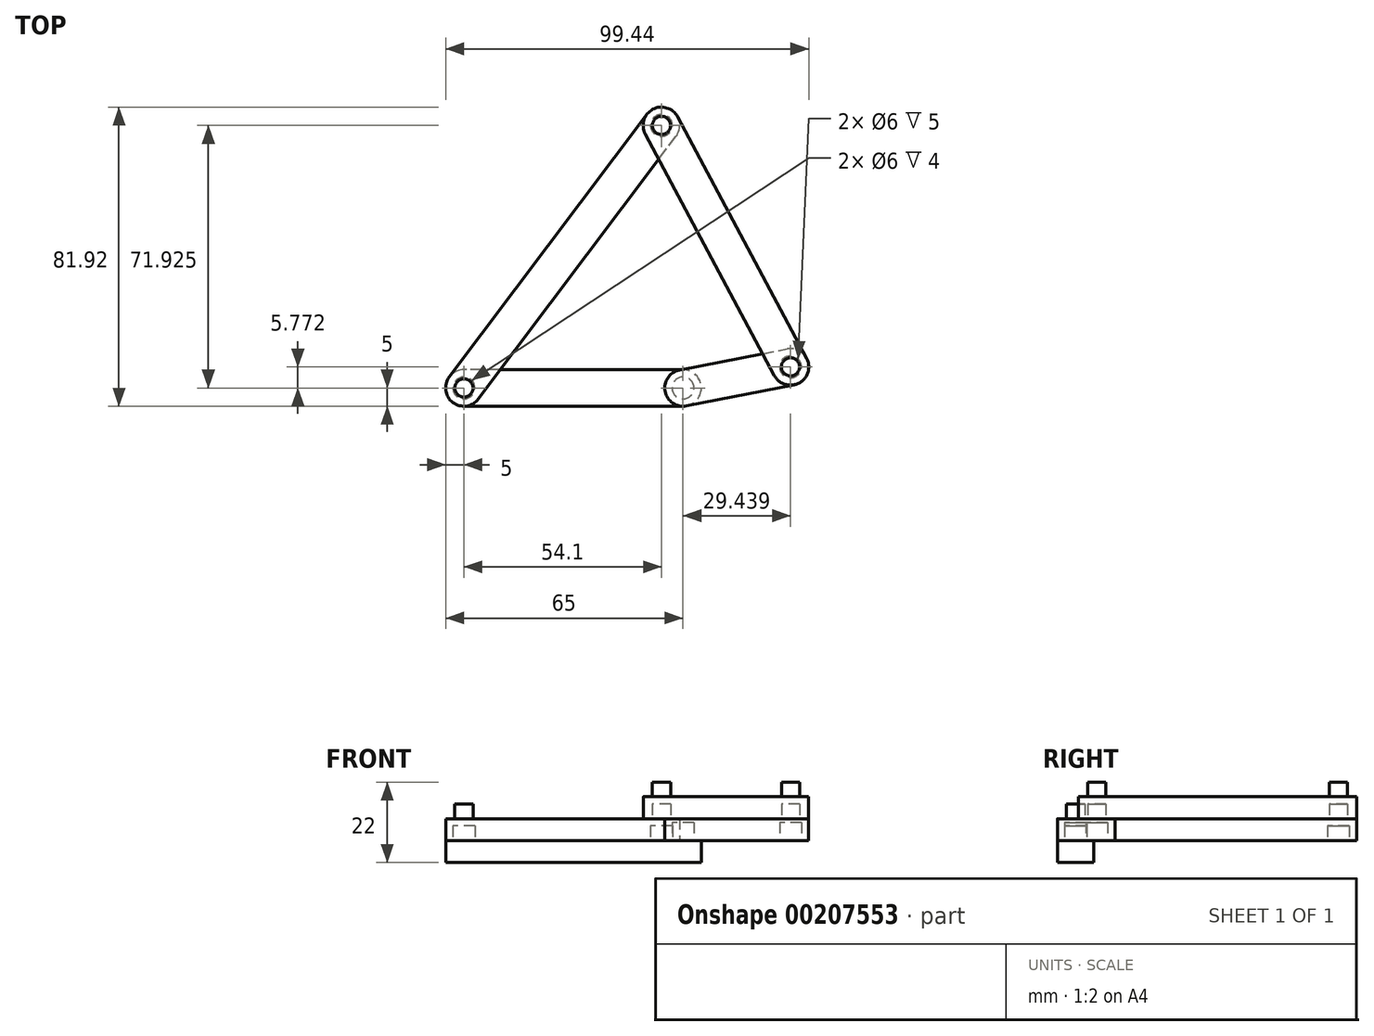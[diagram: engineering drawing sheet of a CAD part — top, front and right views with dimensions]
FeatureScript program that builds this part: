
annotation { "Feature Type Name" : "Feature", "Feature Type Description" : "" }
export const myFeature = defineFeature(function(context is Context, id is Id, definition is map)
    precondition{}
    {
        {
            var Q0;
            Q0=qCreatedBy(makeId("Top.planeOp"),FACE);
            var sketch = newSketch(context, id + "F0", { "sketchPlane" : qUnion([Q0])});
            skLineSegment(sketch, "E0", {"start": v(0, 0) * mm, "end": v(29.44, 5.77) * mm, "construction": true});
            skLineSegment(sketch, "E1", {"start": v(0, 0) * mm, "end": v(-60, 0) * mm, "construction": true});
            skLineSegment(sketch, "E2", {"start": v(-60, 0) * mm, "end": v(-5.9, 71.92) * mm, "construction": true});
            skLineSegment(sketch, "E3", {"start": v(-5.9, 71.92) * mm, "end": v(29.44, 5.77) * mm, "construction": true});
            skSolve(sketch);
        }
        {
            assignVariable(context, id + "F1", {"name" : "HEIGHT", "anyValue" : 6});
        }
        {
            var Q0;
            Q0=qCreatedBy(makeId("Top.planeOp"),FACE);
            cPlane(context, id + "F2", {"entities" : qUnion([Q0]), "cplaneType" : CPlaneType.OFFSET, "offset" : (getVariable(context, 'HEIGHT')) * mm, "width" : 150 * mm, "height" : 150 * mm});
        }
        {
            var Q0;
            Q0=qCreatedBy(id+"F2.planeOp",FACE);
            cPlane(context, id + "F3", {"entities" : qUnion([Q0]), "cplaneType" : CPlaneType.OFFSET, "offset" : (getVariable(context, 'HEIGHT')) * mm, "width" : 150 * mm, "height" : 150 * mm});
        }
        {
            var Q0;
            Q0=qCreatedBy(id+"F3.planeOp",FACE);
            cPlane(context, id + "F4", {"entities" : qUnion([Q0]), "cplaneType" : CPlaneType.OFFSET, "offset" : (getVariable(context, 'HEIGHT')) * mm, "width" : 150 * mm, "height" : 150 * mm});
        }
        {
            var Q0;
            Q0=qCreatedBy(makeId("Top.planeOp"),FACE);
            var sketch = newSketch(context, id + "F5", { "sketchPlane" : qUnion([Q0])});
            skLineSegment(sketch, "E4.JFF.JFF", {"start": v(0, 0) * mm, "end": v(-60, 0) * mm, "construction": true});
            skArc(sketch, "E4.0.startCap", {"start": v(0, 5) * mm, "mid": v(5, 0) * mm, "end": v(0, -5) * mm});
            skArc(sketch, "E4.0.endCap", {"start": v(-60, -5) * mm, "mid": v(-65, 0) * mm, "end": v(-60, 5) * mm});
            skLineSegment(sketch, "E4.0.left", {"start": v(0, -5) * mm, "end": v(-60, -5) * mm});
            skLineSegment(sketch, "E4.0.right", {"start": v(0, 5) * mm, "end": v(-60, 5) * mm});
            skSolve(sketch);
        }
        {
            var Q0;
            Q0=qSketchRegion(id+"F5",true);
            extrude(context, id + "F6", {"entities" : qUnion([Q0]), "depth" : (getVariable(context, 'HEIGHT')) * mm});
        }
        {
            var Q0;
            Q0=qCreatedBy(makeId("Top.planeOp"),FACE);
            var sketch = newSketch(context, id + "F7", { "sketchPlane" : qUnion([Q0])});
            skCircle(sketch, "E5", {"center": v(-60, 0) * mm, "radius": 2.5 * mm});
            skCircle(sketch, "E6", {"center": v(0, 0) * mm, "radius": 2.5 * mm});
            skSolve(sketch);
        }
        {
            var Q0;
            Q0=qSketchRegion(id+"F7",true);
            extrude(context, id + "F8", {"entities" : qUnion([Q0]), "operationType" : NewBodyOperationType.ADD, "depth" : (getVariable(context, 'HEIGHT') * 2 - 2) * mm});
        }
        {
            var Q0;
            Q0=qCreatedBy(makeId("Top.planeOp"),FACE);
            var sketch = newSketch(context, id + "F9", { "sketchPlane" : qUnion([Q0])});
            skCircle(sketch, "E7", {"center": v(-60, 0) * mm, "radius": 3 * mm});
            skCircle(sketch, "E8", {"center": v(0, 0) * mm, "radius": 3 * mm});
            skSolve(sketch);
        }
        {
            var Q0;
            Q0 = qSketchRegion(id + "F9", true);
            extrude(context, id + "F10", {"entities" : qUnion([Q0]), "operationType" : NewBodyOperationType.ADD, "depth" : (getVariable(context, 'HEIGHT') - 1) * mm});
        }
        {
            var Q0;
            Q0=qCreatedBy(id+"F2.planeOp",FACE);
            var sketch = newSketch(context, id + "F11", { "sketchPlane" : qUnion([Q0])});
            skLineSegment(sketch, "E9.JFB.JFB", {"start": v(0, 0) * mm, "end": v(29.44, 5.77) * mm, "construction": true});
            skArc(sketch, "E9.0.startCap", {"start": v(0.96, -4.9) * mm, "mid": v(-4.9, -0.96) * mm, "end": v(-0.96, 4.9) * mm});
            skArc(sketch, "E9.0.endCap", {"start": v(28.48, 10.68) * mm, "mid": v(34.35, 6.73) * mm, "end": v(30.4, 0.87) * mm});
            skLineSegment(sketch, "E9.0.left", {"start": v(-0.96, 4.9) * mm, "end": v(28.48, 10.68) * mm});
            skLineSegment(sketch, "E9.0.right", {"start": v(0.96, -4.9) * mm, "end": v(30.4, 0.87) * mm});
            skSolve(sketch);
        }
        {
            var Q0;
            Q0=qSketchRegion(id+"F11",true);
            extrude(context, id + "F12", {"entities" : qUnion([Q0]), "depth" : (getVariable(context, 'HEIGHT')) * mm});
        }
        {
            var Q0;
            Q0=qCreatedBy(id+"F3.planeOp",FACE);
            var sketch = newSketch(context, id + "F13", { "sketchPlane" : qUnion([Q0])});
            skCircle(sketch, "E10", {"center": v(29.44, 5.77) * mm, "radius": 2.5 * mm});
            skSolve(sketch);
        }
        {
            var Q0;
            Q0 = qSketchRegion(id + "F13", true);
            extrude(context, id + "F14", {"entities" : qUnion([Q0]), "operationType" : NewBodyOperationType.ADD, "depth" : (getVariable(context, 'HEIGHT') - 2) * mm});
        }
        {
            var Q0;
            Q0=qCreatedBy(id+"F2.planeOp",FACE);
            var sketch = newSketch(context, id + "F15", { "sketchPlane" : qUnion([Q0])});
            skCircle(sketch, "E11", {"center": v(0, 0) * mm, "radius": 3 * mm});
            skCircle(sketch, "E12", {"center": v(29.44, 5.77) * mm, "radius": 3 * mm});
            skSolve(sketch);
        }
        {
            var Q0;
            Q0 = qSketchRegion(id + "F15", true);
            extrude(context, id + "F16", {"entities" : qUnion([Q0]), "operationType" : NewBodyOperationType.REMOVE, "depth" : (getVariable(context, 'HEIGHT') - 1) * mm});
        }
        {
            var Q0;
            Q0=qCreatedBy(id+"F2.planeOp",FACE);
            var sketch = newSketch(context, id + "F17", { "sketchPlane" : qUnion([Q0])});
            skLineSegment(sketch, "E13.JFJ.JFJ", {"start": v(-60, 0) * mm, "end": v(-5.9, 71.92) * mm, "construction": true});
            skArc(sketch, "E13.0.startCap", {"start": v(-56, -3) * mm, "mid": v(-63, -4) * mm, "end": v(-64, 3) * mm});
            skArc(sketch, "E13.0.endCap", {"start": v(-9.9, 74.93) * mm, "mid": v(-2.9, 75.92) * mm, "end": v(-1.9, 68.92) * mm});
            skLineSegment(sketch, "E13.0.left", {"start": v(-64, 3) * mm, "end": v(-9.9, 74.93) * mm});
            skLineSegment(sketch, "E13.0.right", {"start": v(-56, -3) * mm, "end": v(-1.9, 68.92) * mm});
            skSolve(sketch);
        }
        {
            var Q0;
            Q0=qSketchRegion(id+"F17",true);
            extrude(context, id + "F18", {"entities" : qUnion([Q0]), "depth" : (getVariable(context, 'HEIGHT')) * mm});
        }
        {
            var Q0;
            Q0=qCreatedBy(id+"F3.planeOp",FACE);
            var sketch = newSketch(context, id + "F19", { "sketchPlane" : qUnion([Q0])});
            skCircle(sketch, "E14", {"center": v(-5.9, 71.92) * mm, "radius": 2.5 * mm});
            skCircle(sketch, "E15", {"center": v(-60, 0) * mm, "radius": 2.5 * mm});
            skSolve(sketch);
        }
        {
            var Q0;
            Q0 = qSketchRegion(id + "F19", true);
            extrude(context, id + "F20", {"entities" : qUnion([Q0]), "operationType" : NewBodyOperationType.ADD, "depth" : (getVariable(context, 'HEIGHT') - 2) * mm});
        }
        {
            var Q0;
            Q0=qCreatedBy(id+"F2.planeOp",FACE);
            var sketch = newSketch(context, id + "F21", { "sketchPlane" : qUnion([Q0])});
            skCircle(sketch, "E16", {"center": v(-60, 0) * mm, "radius": 3 * mm});
            skCircle(sketch, "E17", {"center": v(-5.9, 71.92) * mm, "radius": 3 * mm});
            skSolve(sketch);
        }
        {
            var Q0;
            Q0 = qSketchRegion(id + "F21", true);
            extrude(context, id + "F22", {"entities" : qUnion([Q0]), "operationType" : NewBodyOperationType.REMOVE, "depth" : (getVariable(context, 'HEIGHT') - 2) * mm});
        }
        {
            var Q0;
            Q0=qCreatedBy(id+"F3.planeOp",FACE);
            var sketch = newSketch(context, id + "F23", { "sketchPlane" : qUnion([Q0])});
            skLineSegment(sketch, "E18.0", {"start": v(-5.9, 71.92) * mm, "end": v(29.44, 5.77) * mm, "construction": true});
            skArc(sketch, "E19.0.startCap", {"start": v(-10.3, 69.57) * mm, "mid": v(-8.26, 76.33) * mm, "end": v(-1.49, 74.28) * mm});
            skArc(sketch, "E19.0.endCap", {"start": v(33.85, 8.13) * mm, "mid": v(31.8, 1.36) * mm, "end": v(25.03, 3.42) * mm});
            skLineSegment(sketch, "E19.0.left", {"start": v(-1.49, 74.28) * mm, "end": v(33.85, 8.13) * mm});
            skLineSegment(sketch, "E19.0.right", {"start": v(-10.3, 69.57) * mm, "end": v(25.03, 3.42) * mm});
            skSolve(sketch);
        }
        {
            var Q0;
            Q0 = qSketchRegion(id + "F23", true);
            extrude(context, id + "F24", {"entities" : qUnion([Q0]), "depth" : (getVariable(context, 'HEIGHT')) * mm});
        }
        {
            var Q0;
            Q0=qCreatedBy(id+"F4.planeOp",FACE);
            var sketch = newSketch(context, id + "F25", { "sketchPlane" : qUnion([Q0])});
            skCircle(sketch, "E20", {"center": v(29.44, 5.77) * mm, "radius": 2.5 * mm});
            skCircle(sketch, "E21", {"center": v(-5.9, 71.92) * mm, "radius": 2.5 * mm});
            skSolve(sketch);
        }
        {
            var Q0;
            Q0 = qSketchRegion(id + "F25", true);
            extrude(context, id + "F26", {"entities" : qUnion([Q0]), "operationType" : NewBodyOperationType.ADD, "depth" : (getVariable(context, 'HEIGHT') - 2) * mm});
        }
    });
